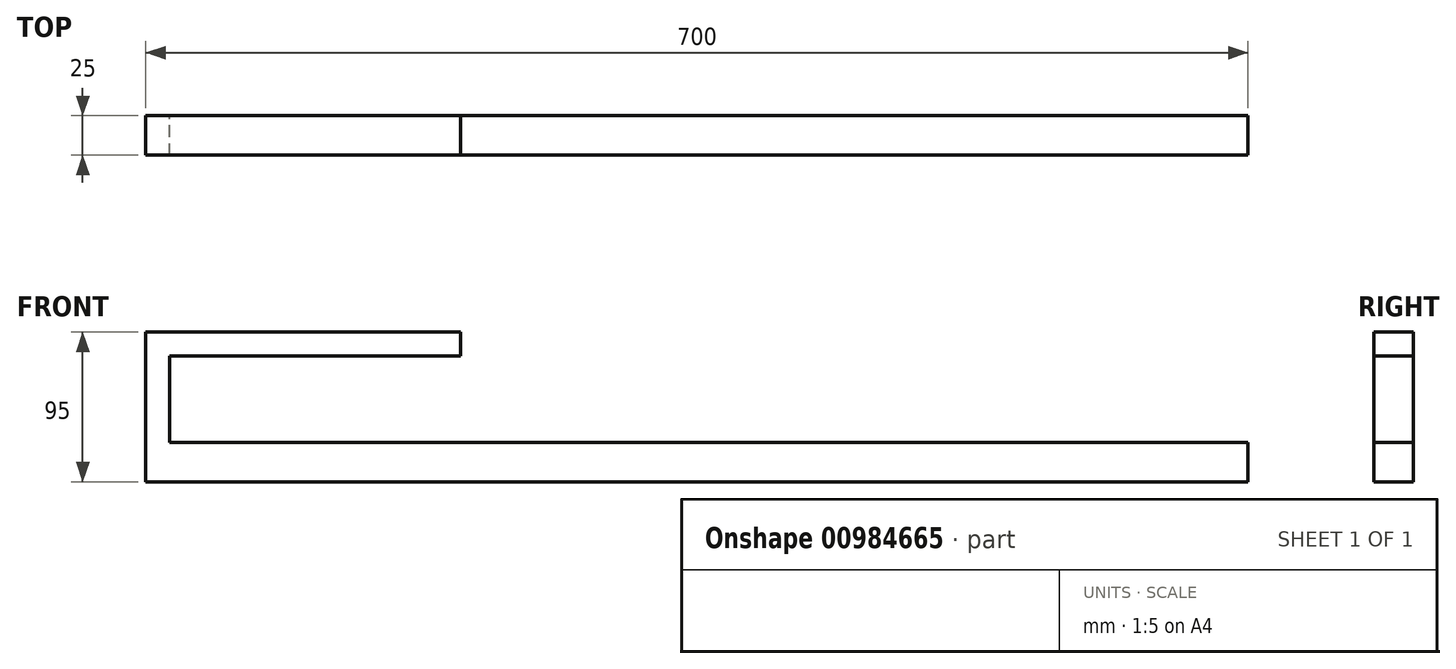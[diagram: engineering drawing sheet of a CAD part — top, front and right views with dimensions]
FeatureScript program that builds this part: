
annotation { "Feature Type Name" : "Feature", "Feature Type Description" : "" }
export const myFeature = defineFeature(function(context is Context, id is Id, definition is map)
    precondition{}
    {
        {
            var Q0;
            Q0=qCreatedBy(makeId("Front.planeOp"),FACE);
            var sketch = newSketch(context, id + "F0", { "sketchPlane" : qUnion([Q0])});
            skLineSegment(sketch, "E0.bottom", {"start": v(0, 0) * mm, "end": v(-700, 0) * mm});
            skLineSegment(sketch, "E0.top", {"start": v(0, 25) * mm, "end": v(-685, 25) * mm});
            skLineSegment(sketch, "E0.left", {"start": v(0, 0) * mm, "end": v(0, 25) * mm});
            skLineSegment(sketch, "E0.right", {"start": v(-700, 0) * mm, "end": v(-700, 25) * mm});
            skLineSegment(sketch, "E1", {"start": v(-700, 25) * mm, "end": v(-700, 95) * mm});
            skLineSegment(sketch, "E2", {"start": v(-700, 95) * mm, "end": v(-500, 95) * mm});
            skLineSegment(sketch, "E3", {"start": v(-500, 95) * mm, "end": v(-500, 80) * mm});
            skLineSegment(sketch, "E4", {"start": v(-500, 80) * mm, "end": v(-685, 80) * mm});
            skLineSegment(sketch, "E5", {"start": v(-685, 80) * mm, "end": v(-685, 25) * mm});
            skSolve(sketch);
        }
        {
            var Q0;
            Q0 = qSketchRegion(id + "F0", true);
            extrude(context, id + "F1", {"entities" : qUnion([Q0]), "depth" : 25 * mm, "offsetDistance" : 25 * mm});
        }
    });
